# Revit family: Reece_Dura_Lead Free_Spring Check Valve
name_source: partatom
category: Pipe Accessories
revit_build: Autodesk Revit 2018 (Build: 20181011_1500(x64)
units: mm (PartAtom-declared; Revit-internal decimal feet)

## family parameters
Always vertical = Yes
Cut with Voids When Loaded = No
OmniClass Number = 23.65.55.14
OmniClass Title = Valves for Liquid Services
Part Type = Valve - Breaks Into
Round Connector Dimension = Use Diameter
Shared = Yes
Work Plane-Based = No

## types (1)
- Standard
    Description = Dura LF Brass Spring Check Valve WM 15mm
    Disclaimer = THIS FILE IS THE PROPERTY OF THE REECE GROUP. IT MAY NOT BE REPRODUCED, REVERSE-ENGINEERED, OR MODIFIED. ANY REPUBLICATION, TRANSMISSION, OR DISTRIBUTION FOR THE PURPOSE OF COMMERCIALLY EXPLOITING THE FILES IS PROHIBITED.
    K Coefficient Table = Tee
    Keynote = Product #1009556, Reece_Dura_Lead Free_Spring Check Valve - Standard
    Loss Method = Not Defined
    Manufacturer = Dura
    Reece_Detail_Disclaimer = THIS FILE IS THE PROPERTY OF THE REECE GROUP. IT MAY NOT BE REPRODUCED, REVERSE-ENGINEERED, OR MODIFIED. ANY REPUBLICATION, TRANSMISSION, OR DISTRIBUTION FOR THE PURPOSE OF COMMERCIALLY EXPLOITING THE FILES IS PROHIBITED.
    Reece_Material_Main = Reece_DR_Brass
    Reece_Material_Secondary = Reece_Plastic_ABS_White
    Reece_Product_Brand = Dura
    Reece_Product_Type = Pipe Fitting
    Type Comments = Pipe Fitting

## geometry (parser evidence)
native form markers: Sweep x1
no freeform markers — native parametric forms only
